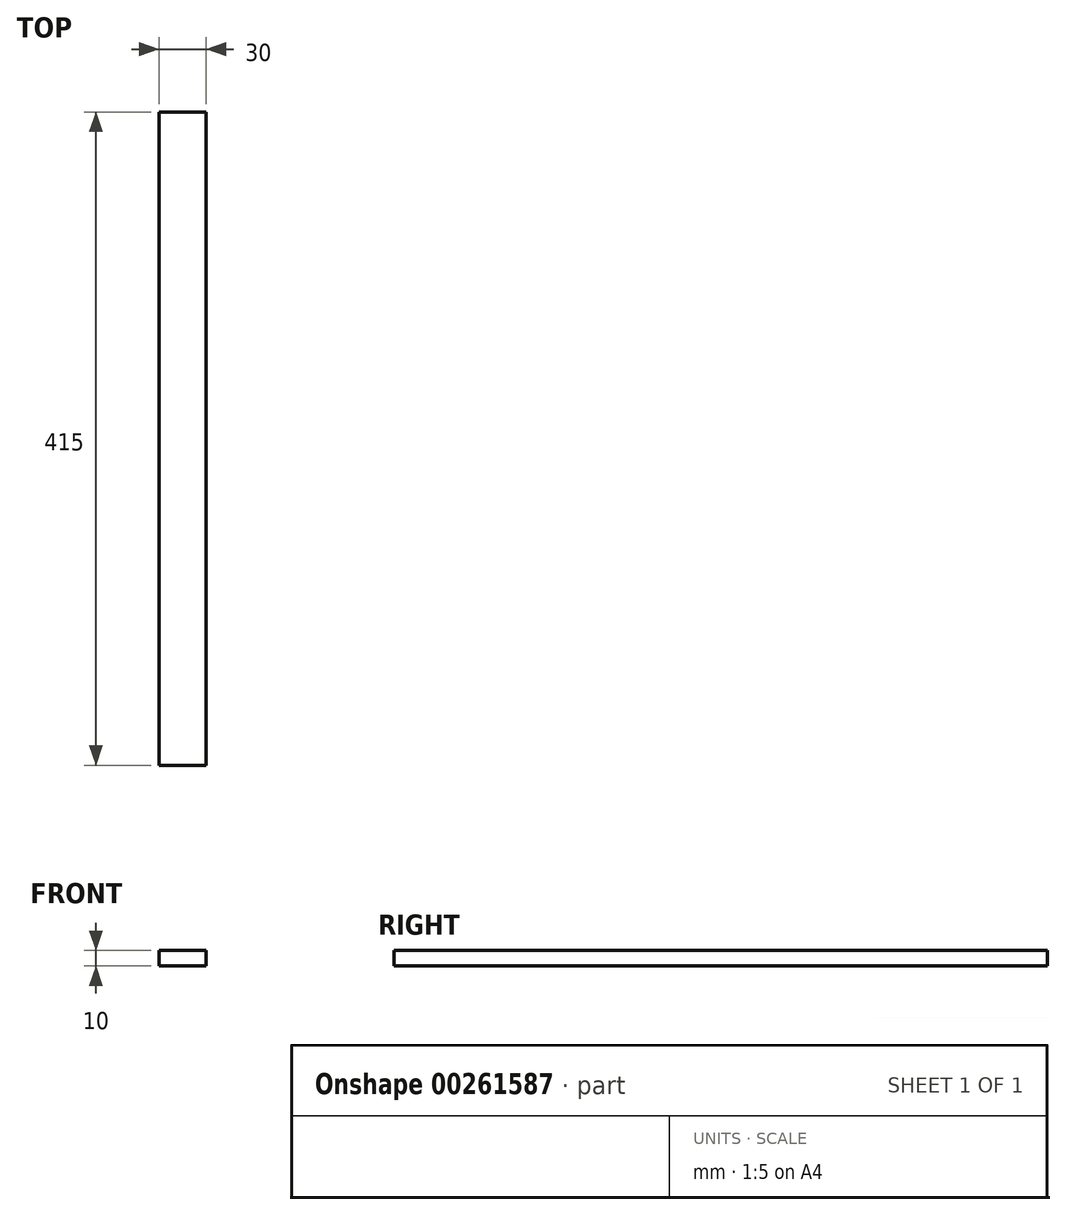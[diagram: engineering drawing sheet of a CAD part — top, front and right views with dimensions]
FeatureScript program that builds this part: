
annotation { "Feature Type Name" : "Feature", "Feature Type Description" : "" }
export const myFeature = defineFeature(function(context is Context, id is Id, definition is map)
    precondition{}
    {
        {
            var Q0;
            Q0=qCreatedBy(makeId("Front.planeOp"),FACE);
            var sketch = newSketch(context, id + "F0", { "sketchPlane" : qUnion([Q0])});
            skLineSegment(sketch, "E0.bottom", {"start": v(0, 0) * mm, "end": v(30, 0) * mm});
            skLineSegment(sketch, "E0.top", {"start": v(0, -10) * mm, "end": v(30, -10) * mm});
            skLineSegment(sketch, "E0.left", {"start": v(0, 0) * mm, "end": v(0, -10) * mm});
            skLineSegment(sketch, "E0.right", {"start": v(30, 0) * mm, "end": v(30, -10) * mm});
            skSolve(sketch);
        }
        {
            var Q0;
            Q0 = qSketchRegion(id + "F0", true);
            extrude(context, id + "F1", {"entities" : qUnion([Q0]), "depth" : 415 * mm});
        }
    });
